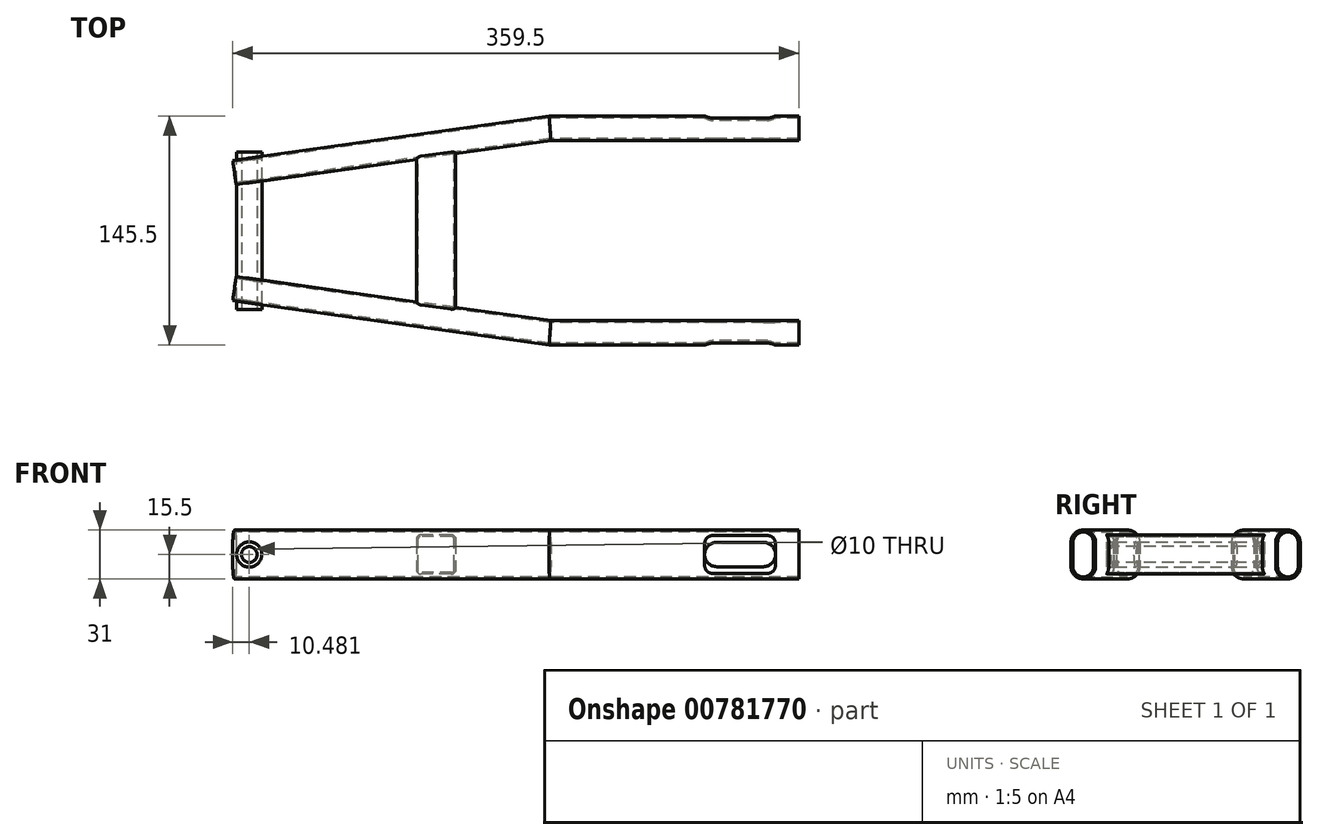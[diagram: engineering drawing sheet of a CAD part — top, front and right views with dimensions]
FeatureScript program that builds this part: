
annotation { "Feature Type Name" : "Feature", "Feature Type Description" : "" }
export const myFeature = defineFeature(function(context is Context, id is Id, definition is map)
    precondition{}
    {
        {
            var Q0;
            Q0=qCreatedBy(makeId("Top.planeOp"),FACE);
            var sketch = newSketch(context, id + "F0", { "sketchPlane" : qUnion([Q0])});
            skLineSegment(sketch, "E0", {"start": v(0, 65) * mm, "end": v(-158.03, 65) * mm});
            skLineSegment(sketch, "E1", {"start": v(-158.03, 65) * mm, "end": v(-358.42, 36.84) * mm});
            skSolve(sketch);
        }
        {
            var Q0;
            Q0=qCreatedBy(makeId("Right.planeOp"),FACE);
            var sketch = newSketch(context, id + "F1", { "sketchPlane" : qUnion([Q0])});
            skLineSegment(sketch, "E2.left", {"start": v(57.25, 7.75) * mm, "end": v(57.25, -7.75) * mm});
            skLineSegment(sketch, "E2.right", {"start": v(72.75, 7.75) * mm, "end": v(72.75, -7.75) * mm});
            skPoint(sketch, "E2.middle", {"position": v(65, 0) * mm});
            skArc(sketch, "E3", {"start": v(57.25, 7.75) * mm, "mid": v(65, 15.5) * mm, "end": v(72.75, 7.75) * mm});
            skArc(sketch, "E4", {"start": v(57.25, -7.75) * mm, "mid": v(65, -15.5) * mm, "end": v(72.75, -7.75) * mm});
            skArc(sketch, "E5.0", {"start": v(58.45, 7.75) * mm, "mid": v(65, 14.3) * mm, "end": v(71.55, 7.75) * mm});
            skLineSegment(sketch, "E6.0", {"start": v(71.55, 7.75) * mm, "end": v(71.55, -7.75) * mm});
            skArc(sketch, "E7.0", {"start": v(58.45, -7.75) * mm, "mid": v(65, -14.3) * mm, "end": v(71.55, -7.75) * mm});
            skLineSegment(sketch, "E8.0", {"start": v(58.45, 7.75) * mm, "end": v(58.45, -7.75) * mm});
            skSolve(sketch);
        }
        {
            var Q0;
            Q0=makeQuery(id+"F1.imprint","IMPRINT",FACE,{"disambiguationData":[TD([[makeQuery(id+"F1.imprint","IMPRINT",EDGE,{"derivedFrom":sQuery(id+"F1.wireOp",EDGE,"E2.left")}),1.0]])]});
            var Q1;
            Q1=sQuery(id+"F0.wireOp",EDGE,"E0");
            var Q2;
            Q2=sQuery(id+"F0.wireOp",EDGE,"E1");
            sweep(context, id + "F2", {"profiles" : qUnion([Q0]), "path" : qUnion([Q1, Q2])});
        }
        {
            var Q0;
            Q0=makeQuery(id+"F2.opSweep","SWEPT_FACE",FACE,{"disambiguationData":[OSD([sQuery(id+"F0.wireOp",EDGE,"E0"),sQuery(id+"F1.wireOp",EDGE,"E2.right")])]});
            var sketch = newSketch(context, id + "F3", { "sketchPlane" : qUnion([Q0])});
            skLineSegment(sketch, "E9.bottom", {"start": v(19.79, 12) * mm, "end": v(54.8, 12) * mm});
            skLineSegment(sketch, "E9.top", {"start": v(19.79, -12) * mm, "end": v(54.8, -12) * mm});
            skLineSegment(sketch, "E9.left", {"start": v(14.79, 7) * mm, "end": v(14.79, -7) * mm});
            skLineSegment(sketch, "E9.right", {"start": v(59.8, 7) * mm, "end": v(59.8, -7) * mm});
            skPoint(sketch, "E9.middle", {"position": v(37.3, 0) * mm});
            skPoint(sketch, "E10.visualSharp", {"position": v(14.79, 12) * mm});
            skArc(sketch, "E10.filletArc", {"start": v(19.79, 12) * mm, "mid": v(16.25, 10.54) * mm, "end": v(14.79, 7) * mm});
            skPoint(sketch, "E11.visualSharp", {"position": v(59.8, 12) * mm});
            skArc(sketch, "E11.filletArc", {"start": v(59.8, 7) * mm, "mid": v(58.33, 10.54) * mm, "end": v(54.8, 12) * mm});
            skPoint(sketch, "E12.visualSharp", {"position": v(59.8, -12) * mm});
            skArc(sketch, "E12.filletArc", {"start": v(54.8, -12) * mm, "mid": v(58.33, -10.54) * mm, "end": v(59.8, -7) * mm});
            skPoint(sketch, "E13.visualSharp", {"position": v(14.79, -12) * mm});
            skArc(sketch, "E13.filletArc", {"start": v(14.79, -7) * mm, "mid": v(16.25, -10.54) * mm, "end": v(19.79, -12) * mm});
            skSolve(sketch);
        }
        {
            var Q0;
            Q0=makeQuery(id+"F2.opSweep","SWEPT_FACE",FACE,{"disambiguationData":[OSD([sQuery(id+"F0.wireOp",EDGE,"E0"),sQuery(id+"F1.wireOp",EDGE,"E2.left")])]});
            var sketch = newSketch(context, id + "F4", { "sketchPlane" : qUnion([Q0])});
            skArc(sketch, "E14.0.0", {"start": v(-52.04, -7.75) * mm, "mid": v(-59.8, 0) * mm, "end": v(-52.04, 7.75) * mm});
            skLineSegment(sketch, "E14.0.1", {"start": v(-52.04, 7.75) * mm, "end": v(-22.54, 7.75) * mm});
            skArc(sketch, "E14.0.2", {"start": v(-22.54, 7.75) * mm, "mid": v(-14.79, 0) * mm, "end": v(-22.54, -7.75) * mm});
            skLineSegment(sketch, "E14.0.3", {"start": v(-22.54, -7.75) * mm, "end": v(-52.04, -7.75) * mm});
            skSolve(sketch);
        }
        {
            var Q0;
            Q0 = qSketchRegion(id + "F4", true);
            extrude(context, id + "F5", {"entities" : qUnion([Q0]), "operationType" : NewBodyOperationType.REMOVE, "oppositeDirection" : true, "depth" : 4 * mm, "offsetDistance" : 25 * mm});
        }
        {
            var Q0;
            Q0 = qSketchRegion(id + "F3", true);
            extrude(context, id + "F6", {"entities" : qUnion([Q0]), "operationType" : NewBodyOperationType.REMOVE, "oppositeDirection" : true, "depth" : 4 * mm, "offsetDistance" : 25 * mm});
        }
        {
            var Q0;
            Q0=makeQuery(id+"F2.opSweep","SWEPT_BODY",BODY,{"disambiguationData":[OSD([sQuery(id+"F0.wireOp",EDGE,"E1"),sQuery(id+"F1.wireOp",EDGE,"E2.left"),sQuery(id+"F1.wireOp",EDGE,"E2.right"),sQuery(id+"F1.wireOp",EDGE,"E3"),sQuery(id+"F1.wireOp",EDGE,"E4"),sQuery(id+"F1.wireOp",EDGE,"E5.0"),sQuery(id+"F1.wireOp",EDGE,"E6.0"),sQuery(id+"F1.wireOp",EDGE,"E7.0"),sQuery(id+"F1.wireOp",EDGE,"E8.0")])]});
            var Q1;
            Q1=qCreatedBy(makeId("Front.planeOp"),FACE);
            mirror(context, id + "F7", {"entities" : qUnion([Q0]), "mirrorPlane" : qUnion([Q1])});
        }
        {
            var Q0;
            Q0=qCreatedBy(makeId("Front.planeOp"),FACE);
            var sketch = newSketch(context, id + "F8", { "sketchPlane" : qUnion([Q0])});
            skCircle(sketch, "E15", {"center": v(-349.02, 0) * mm, "radius": 8 * mm});
            skSolve(sketch);
        }
        {
            var Q0;
            Q0=makeQuery(id+"F8.imprint","IMPRINT",FACE,{"disambiguationData":[TD([[makeQuery(id+"F8.imprint","IMPRINT",EDGE,{"derivedFrom":sQuery(id+"F8.wireOp",EDGE,"E15")}),1.0]])]});
            extrude(context, id + "F9", {"entities" : qUnion([Q0]), "operationType" : NewBodyOperationType.ADD, "endBound" : BoundingType.SYMMETRIC, "depth" : 100 * mm, "offsetDistance" : 25 * mm});
        }
        {
            var Q0;
            Q0=makeQuery(id+"F9.opExtrude","CAP_FACE",FACE,{"disambiguationData":[OSD([sQuery(id+"F8.wireOp",EDGE,"E15")])],"isStart":false});
            var sketch = newSketch(context, id + "F10", { "sketchPlane" : qUnion([Q0])});
            skCircle(sketch, "E16", {"center": v(-349.02, 0) * mm, "radius": 5 * mm});
            skSolve(sketch);
        }
        {
            var Q0;
            Q0 = qSketchRegion(id + "F10", true);
            extrude(context, id + "F11", {"entities" : qUnion([Q0]), "operationType" : NewBodyOperationType.REMOVE, "endBound" : BoundingType.THROUGH_ALL, "oppositeDirection" : true, "depth" : 25 * mm, "offsetDistance" : 25 * mm});
        }
        {
            var Q0;
            Q0=qCreatedBy(makeId("Front.planeOp"),FACE);
            var sketch = newSketch(context, id + "F12", { "sketchPlane" : qUnion([Q0])});
            skLineSegment(sketch, "E17.bottom", {"start": v(-239.9, 12.5) * mm, "end": v(-220.9, 12.5) * mm});
            skLineSegment(sketch, "E17.top", {"start": v(-239.9, -12.5) * mm, "end": v(-220.9, -12.5) * mm});
            skLineSegment(sketch, "E17.left", {"start": v(-242.9, 9.5) * mm, "end": v(-242.9, -9.5) * mm});
            skLineSegment(sketch, "E17.right", {"start": v(-217.9, 9.5) * mm, "end": v(-217.9, -9.5) * mm});
            skPoint(sketch, "E17.middle", {"position": v(-230.4, 0) * mm});
            skLineSegment(sketch, "E18.bottom", {"start": v(-240.4, 11.4) * mm, "end": v(-220.4, 11.4) * mm});
            skLineSegment(sketch, "E18.top", {"start": v(-241.8, -11.4) * mm, "end": v(-220.4, -11.4) * mm});
            skLineSegment(sketch, "E18.left", {"start": v(-241.8, 10) * mm, "end": v(-241.8, -11.4) * mm});
            skLineSegment(sketch, "E18.right", {"start": v(-219, 10) * mm, "end": v(-219, -10) * mm});
            skPoint(sketch, "E19.visualSharp", {"position": v(-242.9, 12.5) * mm});
            skArc(sketch, "E19.filletArc", {"start": v(-239.9, 12.5) * mm, "mid": v(-242.02, 11.62) * mm, "end": v(-242.9, 9.5) * mm});
            skPoint(sketch, "E20.visualSharp", {"position": v(-217.9, 12.5) * mm});
            skArc(sketch, "E20.filletArc", {"start": v(-217.9, 9.5) * mm, "mid": v(-218.78, 11.62) * mm, "end": v(-220.9, 12.5) * mm});
            skPoint(sketch, "E21.visualSharp", {"position": v(-217.9, -12.5) * mm});
            skArc(sketch, "E21.filletArc", {"start": v(-220.9, -12.5) * mm, "mid": v(-218.78, -11.62) * mm, "end": v(-217.9, -9.5) * mm});
            skPoint(sketch, "E22.visualSharp", {"position": v(-242.9, -12.5) * mm});
            skArc(sketch, "E22.filletArc", {"start": v(-242.9, -9.5) * mm, "mid": v(-242.02, -11.62) * mm, "end": v(-239.9, -12.5) * mm});
            skPoint(sketch, "E23.visualSharp", {"position": v(-241.8, 11.4) * mm});
            skArc(sketch, "E23.filletArc", {"start": v(-240.4, 11.4) * mm, "mid": v(-241.4, 10.99) * mm, "end": v(-241.8, 10) * mm});
            skPoint(sketch, "E24.visualSharp", {"position": v(-219, 11.4) * mm});
            skArc(sketch, "E24.filletArc", {"start": v(-219, 10) * mm, "mid": v(-219.41, 10.99) * mm, "end": v(-220.4, 11.4) * mm});
            skPoint(sketch, "E25.visualSharp", {"position": v(-219, -11.4) * mm});
            skArc(sketch, "E25.filletArc", {"start": v(-220.4, -11.4) * mm, "mid": v(-219.41, -10.99) * mm, "end": v(-219, -10) * mm});
            skSolve(sketch);
        }
        {
            var Q0;
            Q0 = qSketchRegion(id + "F12", true);
            extrude(context, id + "F13", {"entities" : qUnion([Q0]), "operationType" : NewBodyOperationType.ADD, "endBound" : BoundingType.UP_TO_NEXT, "depth" : 25 * mm, "offsetDistance" : 25 * mm, "hasSecondDirection" : true, "secondDirectionBound" : SecondDirectionBoundingType.UP_TO_NEXT, "secondDirectionOppositeDirection" : true, "secondDirectionDepth" : 25 * mm});
        }
    });
